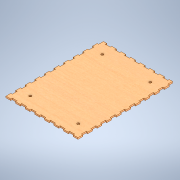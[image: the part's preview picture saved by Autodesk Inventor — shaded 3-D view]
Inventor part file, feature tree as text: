
AUTODESK INVENTOR PART (.ipt)
format: ipt  version: 2021 (Build 250183000, 183)  size: 274,432 bytes
history: native  units: mm
features: extrude x3, sketch x2, other x1
ambient origin geometry x8: Origin, YZ Plane, XZ Plane, XY Plane, X Axis, Y Axis, Z Axis, Center Point
bodies: Body1 (feature_tree)
feature tree (6):
  other  "DoosjeOnderkant"
  extrude  "Extrusion2"  Depth=200.0mm
  extrude  "Extrusion3"  Depth=10.0mm
  extrude  "Extrusion4"  Depth=3.0mm
  sketch  "Sketch3"  dims[d4=150.0mm d5=200.0mm]
  sketch  "Sketch5"  dims[d6=3.0mm d7=0.0mm d8=10.0mm d9=3.0mm d10=10.0mm d11=70.0mm d13=20.0mm d14=10.0mm d16=10.0mm d18=10.0mm d19=3.0mm d20=10.0mm d21=90.0mm d23=20.0mm d24=10.0mm d26=10.0mm d28=10.0mm d29=3.0mm d30=0.0mm d38=5.0mm d39=100.0mm d40=150.0mm d41=2.0mm d42=0.0mm d2=0.5mm d3=0.872665mm]
